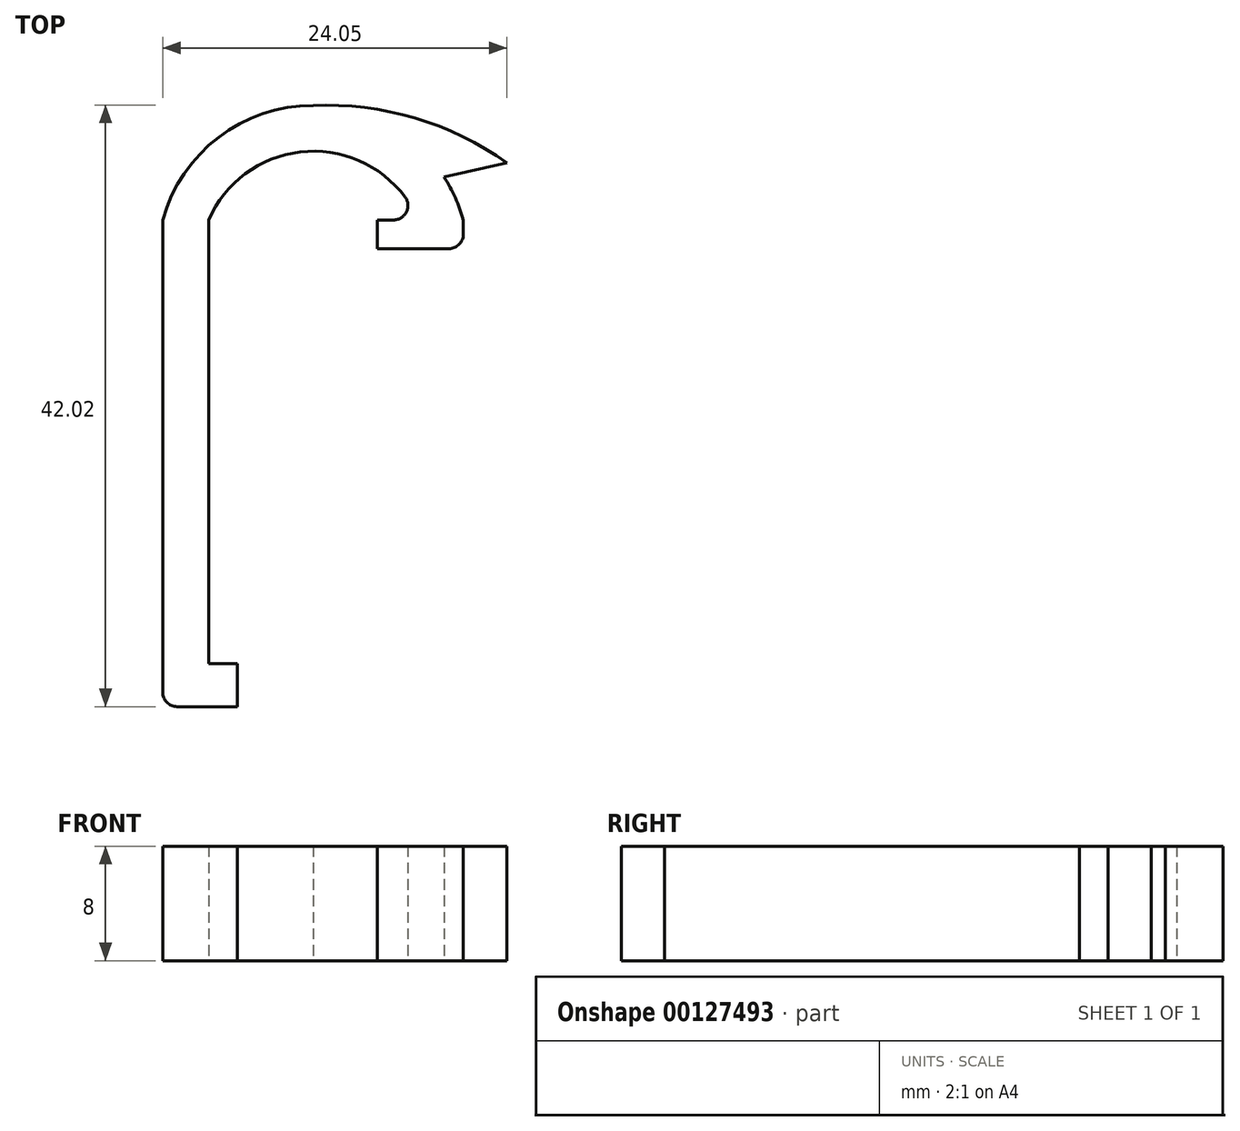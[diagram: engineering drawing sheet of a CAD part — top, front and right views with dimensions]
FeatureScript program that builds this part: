
annotation { "Feature Type Name" : "Feature", "Feature Type Description" : "" }
export const myFeature = defineFeature(function(context is Context, id is Id, definition is map)
    precondition{}
    {
        {
            var Q0;
            Q0=qCreatedBy(makeId("Top.planeOp"),FACE);
            var sketch = newSketch(context, id + "F0", { "sketchPlane" : qUnion([Q0])});
            skLineSegment(sketch, "E0.bottom", {"start": v(1, 0) * mm, "end": v(3.2, 0) * mm});
            skLineSegment(sketch, "E0.top", {"start": v(0, 34) * mm, "end": v(3.2, 34) * mm});
            skLineSegment(sketch, "E0.left", {"start": v(0, 1) * mm, "end": v(0, 34) * mm});
            skLineSegment(sketch, "E0.right", {"start": v(3.2, 0) * mm, "end": v(3.2, 34) * mm});
            skLineSegment(sketch, "E1", {"start": v(3.2, 0) * mm, "end": v(5.2, 0) * mm});
            skLineSegment(sketch, "E2", {"start": v(5.2, 0) * mm, "end": v(5.2, 3) * mm});
            skLineSegment(sketch, "E3", {"start": v(5.2, 3) * mm, "end": v(3.2, 3) * mm});
            skLineSegment(sketch, "E4.bottom", {"start": v(15, 34) * mm, "end": v(16.13, 34) * mm});
            skLineSegment(sketch, "E4.top", {"start": v(15, 32) * mm, "end": v(20, 32) * mm});
            skLineSegment(sketch, "E4.left", {"start": v(15, 34) * mm, "end": v(15, 32) * mm});
            skLineSegment(sketch, "E4.right", {"start": v(21, 34) * mm, "end": v(21, 33) * mm});
            skArc(sketch, "E5", {"start": v(21, 34) * mm, "mid": v(10.5, 42) * mm, "end": v(0, 34) * mm});
            skPoint(sketch, "E6", {"position": v(18, 34) * mm});
            skArc(sketch, "E7", {"start": v(16.93, 35.6) * mm, "mid": v(9.6, 38.75) * mm, "end": v(3.2, 34) * mm});
            skLineSegment(sketch, "E8", {"start": v(19.66, 37) * mm, "end": v(24.05, 38) * mm});
            skArc(sketch, "E9", {"start": v(24.05, 38) * mm, "mid": v(17.6, 41.13) * mm, "end": v(10.5, 42) * mm});
            skPoint(sketch, "E10.newPointA", {"position": v(21, 34) * mm});
            skArc(sketch, "E10.filletArc", {"start": v(16.13, 34) * mm, "mid": v(17.03, 34.55) * mm, "end": v(16.93, 35.6) * mm});
            skPoint(sketch, "E11.visualSharp", {"position": v(21, 32) * mm});
            skArc(sketch, "E11.filletArc", {"start": v(20, 32) * mm, "mid": v(20.7, 32.3) * mm, "end": v(21, 33) * mm});
            skPoint(sketch, "E12.visualSharp", {"position": v(0, 0) * mm});
            skArc(sketch, "E12.filletArc", {"start": v(0, 1) * mm, "mid": v(0.3, 0.3) * mm, "end": v(1, 0) * mm});
            skSolve(sketch);
        }
        {
            var Q0;
            {var subQ0=sQuery(id+"F0.wireOp",EDGE,"E8");Q0=makeQuery(id+"F0.imprint","IMPRINT",FACE,{"disambiguationData":[TD([[makeQuery(id+"F0.imprint","IMPRINT",EDGE,{"derivedFrom":subQ0}),1.0]])]});}
            var Q1;
            Q1=makeQuery(id+"F0.imprint","IMPRINT",FACE,{"disambiguationData":[TD([[makeQuery(id+"F0.imprint","IMPRINT",EDGE,{"derivedFrom":sQuery(id+"F0.wireOp",EDGE,"E4.top")}),1.0]])]});
            var Q2;
            {var subQ0=sQuery(id+"F0.wireOp",EDGE,"E1");Q2=makeQuery(id+"F0.imprint","IMPRINT",FACE,{"disambiguationData":[TD([[makeQuery(id+"F0.imprint","IMPRINT",EDGE,{"derivedFrom":subQ0}),1.0]])]});}
            var Q3;
            {var subQ1=sQuery(id+"F0.wireOp",EDGE,"E0.bottom");Q3=makeQuery(id+"F0.imprint","IMPRINT",FACE,{"disambiguationData":[TD([[makeQuery(id+"F0.imprint","IMPRINT",EDGE,{"derivedFrom":subQ1}),1.0]])]});}
            var Q4;
            {var subQ6=sQuery(id+"F0.wireOp",EDGE,"E0.top");Q4=makeQuery(id+"F0.imprint","IMPRINT",FACE,{"disambiguationData":[TD([[makeQuery(id+"F0.imprint","IMPRINT",EDGE,{"derivedFrom":subQ6}),1.0]])]});}
            extrude(context, id + "F1", {"entities" : qUnion([Q0, Q1, Q2, Q3, Q4]), "depth" : 8 * mm, "offsetDistance" : 25 * mm});
        }
    });
